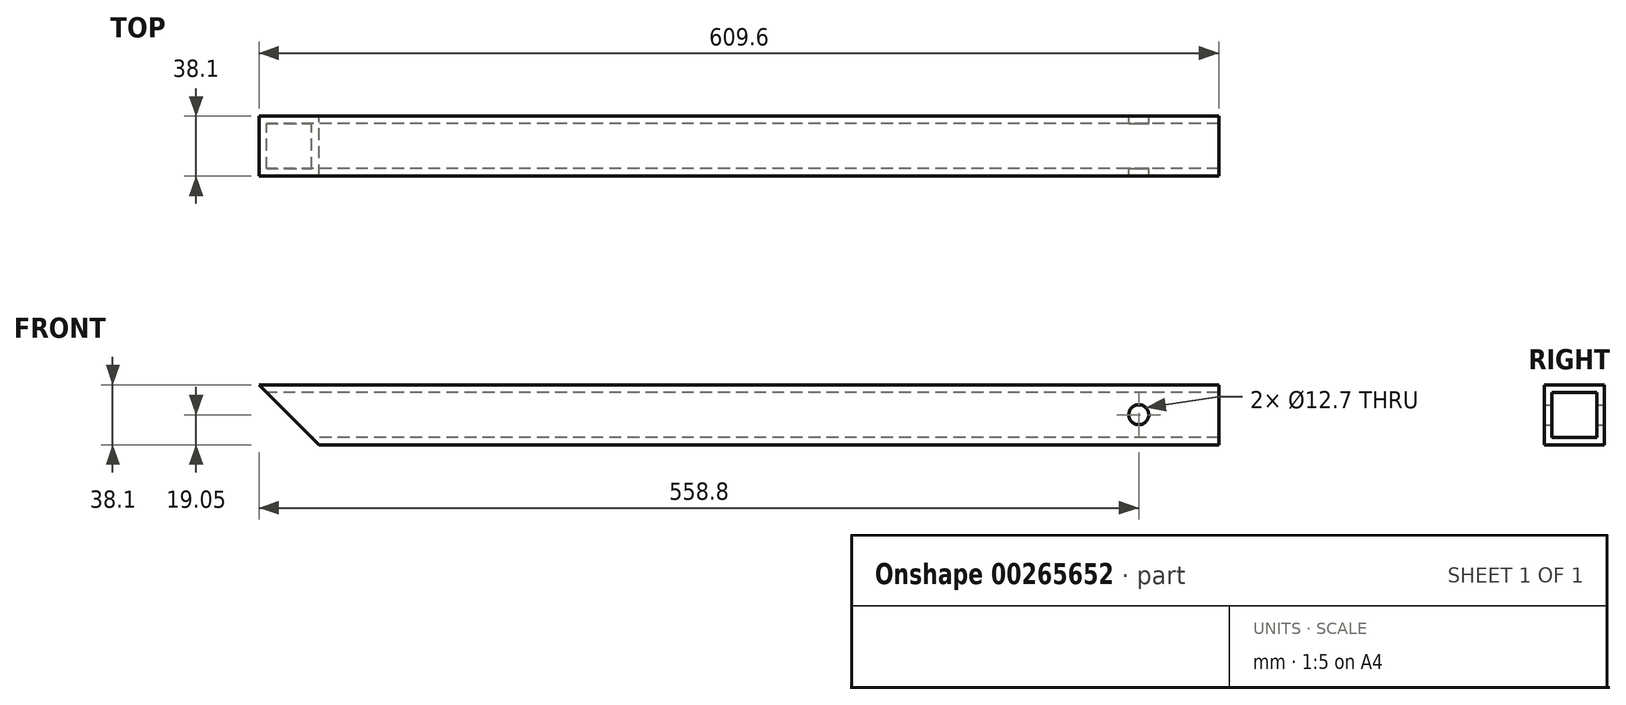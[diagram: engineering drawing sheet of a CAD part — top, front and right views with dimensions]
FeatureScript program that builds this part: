
annotation { "Feature Type Name" : "Feature", "Feature Type Description" : "" }
export const myFeature = defineFeature(function(context is Context, id is Id, definition is map)
    precondition{}
    {
        {
            var Q0;
            Q0=qCreatedBy(makeId("Right.planeOp"),FACE);
            var sketch = newSketch(context, id + "F0", { "sketchPlane" : qUnion([Q0])});
            skLineSegment(sketch, "E0.bottom", {"start": v(-19.05, 19.05) * mm, "end": v(19.05, 19.05) * mm});
            skLineSegment(sketch, "E0.top", {"start": v(-19.05, -19.05) * mm, "end": v(19.05, -19.05) * mm});
            skLineSegment(sketch, "E0.left", {"start": v(-19.05, 19.05) * mm, "end": v(-19.05, -19.05) * mm});
            skLineSegment(sketch, "E0.right", {"start": v(19.05, 19.05) * mm, "end": v(19.05, -19.05) * mm});
            skLineSegment(sketch, "E1.0", {"start": v(-14.27, 14.27) * mm, "end": v(14.27, 14.27) * mm});
            skLineSegment(sketch, "E1.1", {"start": v(-14.27, 14.27) * mm, "end": v(-14.27, -14.27) * mm});
            skLineSegment(sketch, "E1.2", {"start": v(-14.27, -14.27) * mm, "end": v(14.27, -14.27) * mm});
            skLineSegment(sketch, "E1.3", {"start": v(14.27, 14.27) * mm, "end": v(14.27, -14.27) * mm});
            skSolve(sketch);
        }
        {
            var Q0;
            Q0 = qSketchRegion(id + "F0", true);
            extrude(context, id + "F1", {"entities" : qUnion([Q0]), "depth" : 609.6 * mm});
        }
        {
            var Q0;
            Q0=makeQuery(id+"F1.opExtrude","SWEPT_FACE",FACE,{"disambiguationData":[OSD([sQuery(id+"F0.wireOp",EDGE,"E0.right")])]});
            var sketch = newSketch(context, id + "F2", { "sketchPlane" : qUnion([Q0])});
            skLineSegment(sketch, "E2", {"start": v(0, 19.05) * mm, "end": v(-38.1, -19.05) * mm});
            skSolve(sketch);
        }
        {
            var Q0;
            {var subQ0=sQuery(id+"F2.wireOp",EDGE,"E2");Q0=makeQuery(id+"F2.imprint","IMPRINT",FACE,{"disambiguationData":[TD([[makeQuery(id+"F2.imprint","IMPRINT",EDGE,{"derivedFrom":subQ0}),1.0]])]});}
            extrude(context, id + "F3", {"entities" : qUnion([Q0]), "operationType" : NewBodyOperationType.REMOVE, "endBound" : BoundingType.THROUGH_ALL, "oppositeDirection" : true, "depth" : 25.4 * mm});
        }
        {
            var Q0;
            Q0=makeQuery(id+"F1.opExtrude","SWEPT_FACE",FACE,{"disambiguationData":[OSD([sQuery(id+"F0.wireOp",EDGE,"E0.right")])]});
            var sketch = newSketch(context, id + "F4", { "sketchPlane" : qUnion([Q0])});
            skCircle(sketch, "E3", {"center": v(-558.8, 0) * mm, "radius": 6.35 * mm});
            skSolve(sketch);
        }
        {
            var Q0;
            Q0=makeQuery(id+"F4.imprint","IMPRINT",FACE,{"disambiguationData":[TD([[makeQuery(id+"F4.imprint","IMPRINT",EDGE,{"derivedFrom":sQuery(id+"F4.wireOp",EDGE,"E3")}),1.0]])]});
            extrude(context, id + "F5", {"entities" : qUnion([Q0]), "operationType" : NewBodyOperationType.REMOVE, "endBound" : BoundingType.THROUGH_ALL, "oppositeDirection" : true, "depth" : 25.4 * mm});
        }
    });
